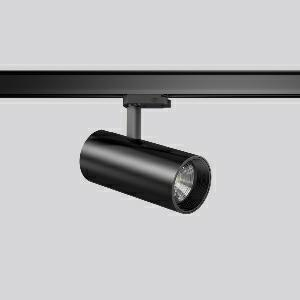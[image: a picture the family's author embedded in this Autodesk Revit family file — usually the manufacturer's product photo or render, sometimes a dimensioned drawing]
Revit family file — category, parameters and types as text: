
# Revit family: deecos_s_mini_742200_003_1_76_500c
name_source: partatom
category: Lighting Fixtures
units: mm (PartAtom-declared; Revit-internal decimal feet)

## family parameters
Cut with Voids When Loaded = No
Host = Face
Light Source = No
Part Type = Normal
Room Calculation Point = No
Round Connector Dimension = Use Diameter
Shared = No

## types (1)
- DEECOS S mini (1 x LED Modul 940, 2150 lm, 4000)
    Apparent Load = 20 VA
    Approval mark = CE
    CIE Flux Codes = 98 100 100 100 100
    Color Rendering = 92
    Color Temperature = 4000
    Default Elevation = 1800 mm
    Description = Series: DEECOS S mini
LED surface-mounted projector in modern design with no visible cooling ribs. Housing: die-cast aluminium, powder-coated. Rotation range: 356°. Swivel range: 90°. Black plastic ring and recessed LED to prevent glare from the side. Optical assembly with lens made of plastic (polycarbonate) for the best homogeneous light distribution - can be changed without tools. Best colour rendering index Ra>90. With adapter for RZB 3-circuit DALI tracks. Suitable for Track on ceiling, Wall track. High quality converter without flickering and stroboscopic effect. The following accessories can be mounted without use of tools: interchangeable lenses, decorative glasses, honeycomb louvre, clear and frosted diffusers, white interchangeable plastic ring. 
Colour: deep black, matt (RAL 9005)
Diameter: 87 mm
Height: 214 mm
Lamp: LED
Socket: without socket
Colour temperature: 4000K
Colour rendering index (CRI): 92
System power: 20 W
Rated luminous flux: 2150 lm
Luminous efficiency: 108 lm/W
Control gear: Converter, dimmable, DALI
Protection class: I
Type of protection: IP 20
    Height = 214 mm
    Lamp = 1 x LED Modul 940
    Lamp Light Flux = 2150 lm
    Lamp count = 1
    Length = 87 mm
    Lifetime = 50000 h
    Luminous efficacy = 108 lm/W
    Manufacturer = RZB
    ModVariant = No
    Model = 742200.003.1.76
    Mounting Place = Ceiling
    Mounting Type = Rail mounted
    Number of Poles = 1
    OnlyDefault = Yes
    Power Factor = 1
    Product Name = DEECOS S mini
    Product group = Track mounted projectors
    ProductGroupID = 301
    Protection Class = Protection class I
    Protection Degree = IP 20
    RLX_Detail_Level = 1
    RLX_Emergency_Light_Flux = 0 lm
    RLX_Emergency_Type = 0
    RLX_Emergency_Type_DB = No
    RlxData = <blob elided: 38753 chars, md5=de8a8cd9>
    Socket = socket
    Standby Power = 0 W
    System Light Flux = 2150 lm
    System Power = 20 W
    Type Comments = Product without accessories
    Type Image = 741930.003.jpg
    URL = http://relux.com
    VarID = ---
    Voltage = 230 V
    Voltage Range = 220-240 V
    Weight = 0.00 kg
    Width = 0 mm  [stored 0 ft]

note: [stored X ft] marks values corroborated as IEEE doubles in the binary element streams (Revit-internal decimal feet)

## geometry (parser evidence)
native form markers: Blend x4, Sweep x12
no freeform markers — native parametric forms only
